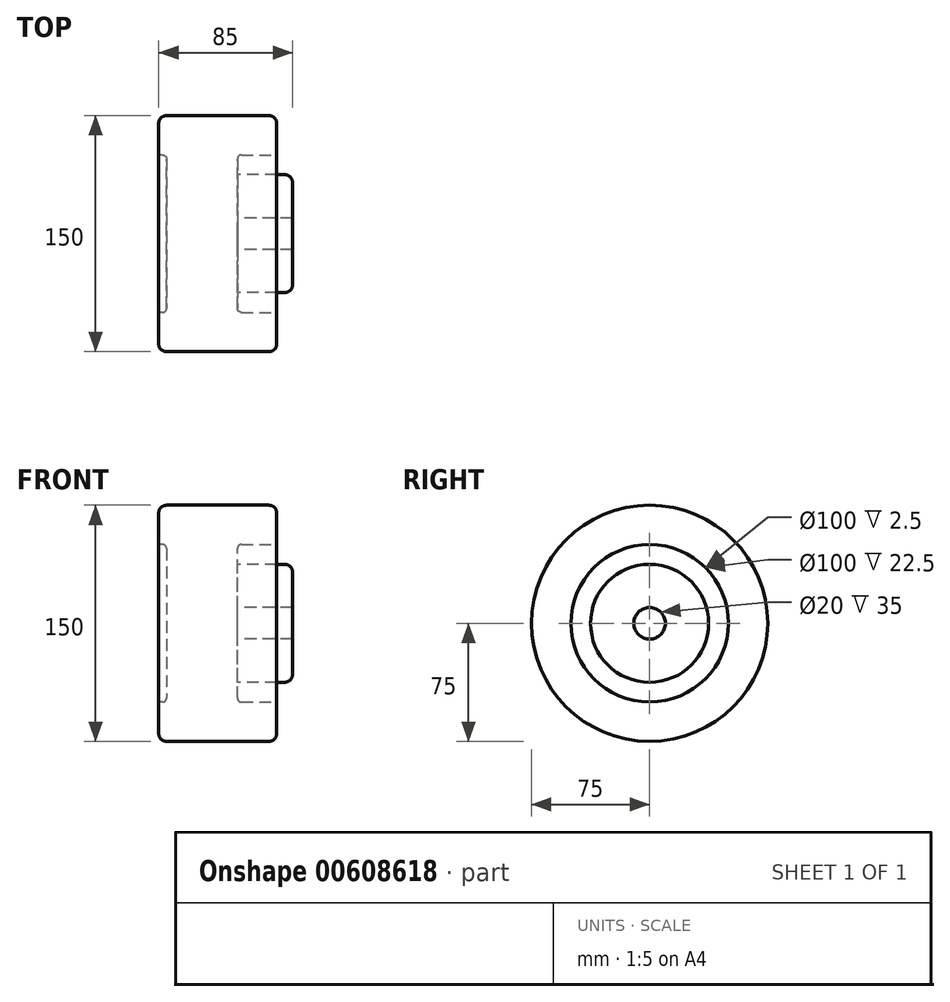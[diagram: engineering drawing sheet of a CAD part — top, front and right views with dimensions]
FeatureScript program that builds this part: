
annotation { "Feature Type Name" : "Feature", "Feature Type Description" : "" }
export const myFeature = defineFeature(function(context is Context, id is Id, definition is map)
    precondition{}
    {
        {
            var Q0;
            Q0=qCreatedBy(makeId("Right.planeOp"),FACE);
            var sketch = newSketch(context, id + "F0", { "sketchPlane" : qUnion([Q0])});
            skCircle(sketch, "E0", {"center": v(0, 0) * mm, "radius": 75 * mm});
            skSolve(sketch);
        }
        {
            var Q0;
            Q0 = qSketchRegion(id + "F0", true);
            extrude(context, id + "F1", {"entities" : qUnion([Q0]), "depth" : 75 * mm, "offsetDistance" : 25 * mm});
        }
        {
            var Q0;
            Q0=makeQuery(id+"F1.opExtrude","SWEPT_FACE",FACE,{"disambiguationData":[OSD([sQuery(id+"F0.wireOp",EDGE,"E0")])]});
            fillet(context, id + "F2", {"entities" : qUnion([Q0]), "radius" : 5 * mm, "tangentPropagation" : true, "allowEdgeOverflow" : false});
        }
        {
            var Q0;
            Q0=makeQuery(id+"F1.opExtrude","CAP_FACE",FACE,{"disambiguationData":[OSD([sQuery(id+"F0.wireOp",EDGE,"E0")])],"isStart":true});
            var sketch = newSketch(context, id + "F3", { "sketchPlane" : qUnion([Q0])});
            skCircle(sketch, "E1", {"center": v(0, 0) * mm, "radius": 50 * mm});
            skSolve(sketch);
        }
        {
            var Q0;
            Q0=makeQuery(id+"F3.imprint","IMPRINT",FACE,{"disambiguationData":[TD([[makeQuery(id+"F3.imprint","IMPRINT",EDGE,{"derivedFrom":sQuery(id+"F3.wireOp",EDGE,"E1")}),1.0]])]});
            extrude(context, id + "F4", {"entities" : qUnion([Q0]), "operationType" : NewBodyOperationType.REMOVE, "oppositeDirection" : true, "depth" : 5 * mm, "offsetDistance" : 25 * mm});
        }
        {
            var Q0;
            Q0=makeQuery(id+"F4.boolean.opBoolean","COPY",EDGE,{"derivedFrom":makeQuery(id+"F4.opExtrude","CAP_EDGE",EDGE,{"disambiguationData":[OSD([sQuery(id+"F3.wireOp",EDGE,"E1")])],"isStart":false})});
            var Q1;
            Q1=makeQuery(id+"F4.boolean.opBoolean","COPY",EDGE,{"derivedFrom":makeQuery(id+"F4.opExtrude","CAP_EDGE",EDGE,{"disambiguationData":[OSD([sQuery(id+"F3.wireOp",EDGE,"E1")])],"isStart":true})});
            fillet(context, id + "F5", {"entities" : qUnion([Q0, Q1]), "radius" : 2.5 * mm, "tangentPropagation" : true, "allowEdgeOverflow" : false});
        }
        {
            var Q0;
            Q0=makeQuery(id+"F1.opExtrude","CAP_FACE",FACE,{"disambiguationData":[OSD([sQuery(id+"F0.wireOp",EDGE,"E0")])],"isStart":false});
            var sketch = newSketch(context, id + "F6", { "sketchPlane" : qUnion([Q0])});
            skCircle(sketch, "E2", {"center": v(0, 0) * mm, "radius": 50 * mm});
            skSolve(sketch);
        }
        {
            var Q0;
            Q0=makeQuery(id+"F6.imprint","IMPRINT",FACE,{"disambiguationData":[TD([[makeQuery(id+"F6.imprint","IMPRINT",EDGE,{"derivedFrom":sQuery(id+"F6.wireOp",EDGE,"E2")}),1.0]])]});
            extrude(context, id + "F7", {"entities" : qUnion([Q0]), "operationType" : NewBodyOperationType.REMOVE, "oppositeDirection" : true, "depth" : 25 * mm, "offsetDistance" : 25 * mm});
        }
        {
            var Q0;
            Q0=makeQuery(id+"F7.boolean.opBoolean","COPY",EDGE,{"derivedFrom":makeQuery(id+"F7.opExtrude","CAP_EDGE",EDGE,{"disambiguationData":[OSD([sQuery(id+"F6.wireOp",EDGE,"E2")])],"isStart":false})});
            var Q1;
            Q1=makeQuery(id+"F7.boolean.opBoolean","COPY",EDGE,{"derivedFrom":makeQuery(id+"F7.opExtrude","CAP_EDGE",EDGE,{"disambiguationData":[OSD([sQuery(id+"F6.wireOp",EDGE,"E2")])],"isStart":true})});
            fillet(context, id + "F8", {"entities" : qUnion([Q0, Q1]), "radius" : 2.5 * mm, "tangentPropagation" : true, "allowEdgeOverflow" : false});
        }
        {
            var Q0;
            Q0=makeQuery(id+"F7.boolean.opBoolean","COPY",FACE,{"derivedFrom":makeQuery(id+"F7.opExtrude","CAP_FACE",FACE,{"disambiguationData":[OSD([sQuery(id+"F6.wireOp",EDGE,"E2")])],"isStart":false})});
            var sketch = newSketch(context, id + "F9", { "sketchPlane" : qUnion([Q0])});
            skCircle(sketch, "E3", {"center": v(0, 0) * mm, "radius": 37.5 * mm});
            skCircle(sketch, "E4", {"center": v(0, 0) * mm, "radius": 10 * mm});
            skSolve(sketch);
        }
        {
            var Q0;
            Q0=makeQuery(id+"F9.imprint","IMPRINT",FACE,{"disambiguationData":[TD([[makeQuery(id+"F9.imprint","IMPRINT",EDGE,{"derivedFrom":sQuery(id+"F9.wireOp",EDGE,"E3")}),1.0]])]});
            extrude(context, id + "F10", {"entities" : qUnion([Q0]), "operationType" : NewBodyOperationType.ADD, "depth" : 35 * mm, "offsetDistance" : 25 * mm});
        }
        {
            var Q0;
            Q0=makeQuery(id+"F10.opExtrude","CAP_EDGE",EDGE,{"disambiguationData":[OSD([sQuery(id+"F9.wireOp",EDGE,"E3")])],"isStart":true});
            var Q1;
            Q1=makeQuery(id+"F10.opExtrude","CAP_EDGE",EDGE,{"disambiguationData":[OSD([sQuery(id+"F9.wireOp",EDGE,"E3")])],"isStart":false});
            fillet(context, id + "F11", {"entities" : qUnion([Q0, Q1]), "radius" : 5 * mm, "tangentPropagation" : true, "allowEdgeOverflow" : false});
        }
    });
